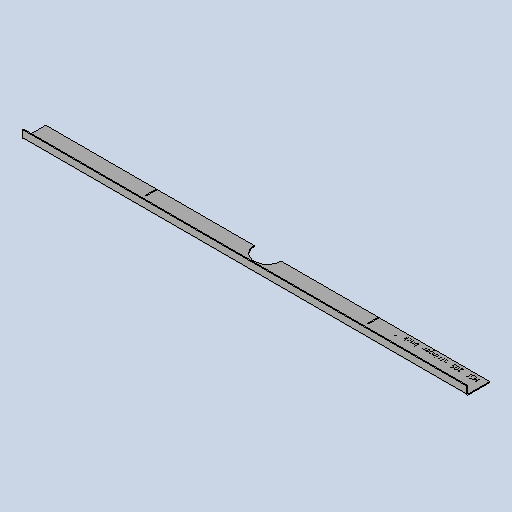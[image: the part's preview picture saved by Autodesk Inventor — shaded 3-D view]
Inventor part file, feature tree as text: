
AUTODESK INVENTOR PART (.ipt)
format: ipt  version: 2025 (Build 290162010, 162A)  size: 278,528 bytes
history: native  units: mm
features: other x5, sheet_metal_op x4, sketch x4, extrude x1
ambient origin geometry x8: Origin, YZ Plane, XZ Plane, XY Plane, X Axis, Y Axis, Z Axis, Center Point
bodies: Solid1 (feature_tree)
feature tree (14):
  sheet_metal_op  "Face1"
  sheet_metal_op  "Flange1"
  extrude  "Extrusion4"  Depth=52.0mm
  other  "Mark3"
  other  "A-Side Definition"
  sketch  "Sketch1"  dims[d0=980.0mm d1=52.0mm]
  other  "Plate1"
  sketch  "Sketch2"  dims[d2=2.0mm]
  other  "Plate2"
  sheet_metal_op  "Bend1"
  sheet_metal_op  "Corner1"
  sketch  "Sketch9"  dims[d3=2.0mm]
  sketch  "Sketch11"  dims[d4=1.0mm d5=4.0mm d6=2.75mm d7=20.0mm d8=90.0deg d9=2.75mm d10=8.0mm d11=2.0mm d12=2.75mm d38=200.0mm d39=12.0mm d42=5.0mm d43=5.0mm d44=60.0mm d45=0.0mm d46=0.0mm d47=2.1mm d49=490.0mm d50=29.0mm]
  other  "Definition1"
